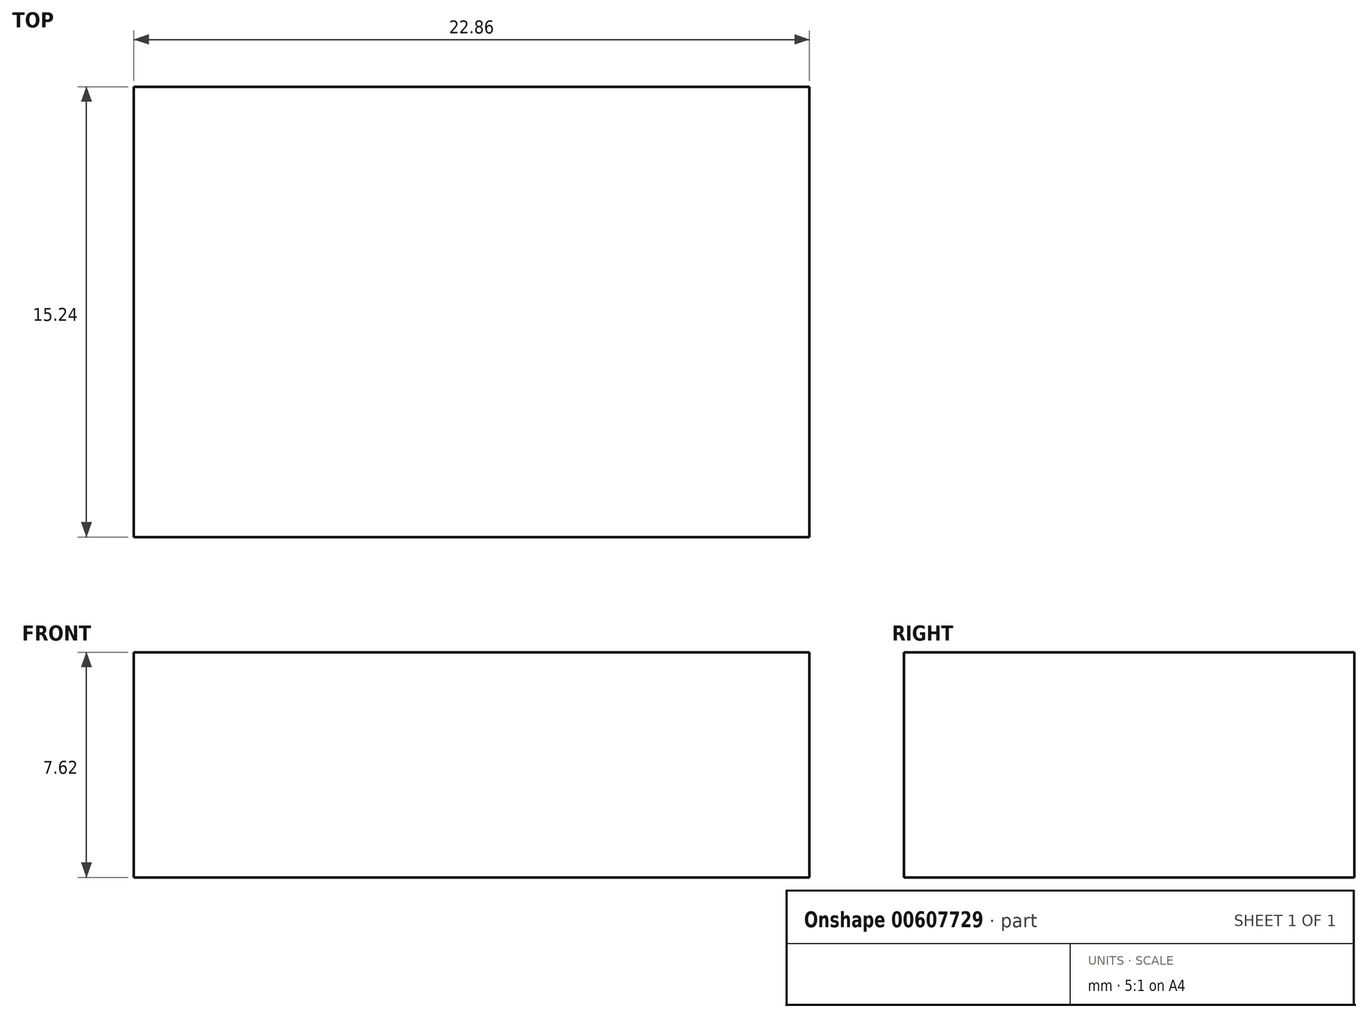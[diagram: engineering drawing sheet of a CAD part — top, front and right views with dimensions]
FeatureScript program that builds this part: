
annotation { "Feature Type Name" : "Feature", "Feature Type Description" : "" }
export const myFeature = defineFeature(function(context is Context, id is Id, definition is map)
    precondition{}
    {
        {
            var Q0;
            Q0=qCreatedBy(makeId("Top.planeOp"),FACE);
            var sketch = newSketch(context, id + "F0", { "sketchPlane" : qUnion([Q0])});
            skLineSegment(sketch, "E0.bottom", {"start": v(-20.26, 24.34) * mm, "end": v(2.6, 24.34) * mm});
            skLineSegment(sketch, "E0.top", {"start": v(-20.26, 39.58) * mm, "end": v(2.6, 39.58) * mm});
            skLineSegment(sketch, "E0.left", {"start": v(-20.26, 24.34) * mm, "end": v(-20.26, 39.58) * mm});
            skLineSegment(sketch, "E0.right", {"start": v(2.6, 24.34) * mm, "end": v(2.6, 39.58) * mm});
            skSolve(sketch);
        }
        {
            var Q0;
            Q0 = qSketchRegion(id + "F0", true);
            extrude(context, id + "F1", {"entities" : qUnion([Q0]), "depth" : 7.62 * mm, "offsetDistance" : 25.4 * mm});
        }
    });
